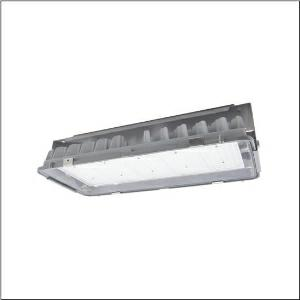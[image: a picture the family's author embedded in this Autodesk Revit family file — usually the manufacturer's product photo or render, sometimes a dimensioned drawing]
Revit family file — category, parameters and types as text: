
# Revit family: highbay_11xtreme_51hf82da4nma
name_source: partatom
category: Lighting Fixtures
units: mm (PartAtom-declared; Revit-internal decimal feet)

## family parameters
Cut with Voids When Loaded = No
Host = Face
Light Source = No
Part Type = Normal
Room Calculation Point = No
Round Connector Dimension = Use Diameter
Shared = No

## types (1)
- --- (1 x LED, 33700 lm, 187.7 W, 4000K)
    Apparent Load = 188 VA
    CIE Flux Codes = 84 96 100 100 100
    Color Rendering = 80
    Color Temperature = 4000K
    Default Elevation = 1800 mm
    Description = Highbay 11Xtreme, high bay luminaire, primary light control with lens, of PMMA, primary optical cover: cover, of toughened safety glass, light emission: direct distribution, primary light characteristic: symmetric, installation type: suspended mounting, surface-mounted, 1x LED module,for 1x LED, rated luminous flux: 33.700lm, luminous efficacy: 180lm/W, light colour: 840, colour temperature: 4000K, control gear: DALI 2, with cable H07RN-F 5x 1.5mm², mains connection: 220..240V, AC, 50/60Hz, cable length: 1,5m, rated input power: 188W, luminaire housing, of diecast aluminium, partly coated, silver, length: 595mm, width: 280mm, height: 195mm, protection rating (complete): IP66, insulation class (complete): insulation class I (protective earthing), certification: CE, ENEC, UKCA, protection symbol: D, ball protection: ball impact resistant according to DIN VDE 0710 part 13 (with chain suspension), impact resistance: IK08, permissible operating ambient temperature: -25..+45°C, reducing of maximum allowable ambient temperature of 5°C with ceiling mounting, packaging unit: 1 piece
    Height = 157 mm
    Lamp = 1 x LED
    Lamp Light Flux = 33700 lm
    Lamp Power = 187.7 W
    Lamp count = 1
    Length = 593 mm
    Luminous efficacy = 180 lm/W
    Manufacturer = Siteco
    ModVariant = No
    Model = 51HF82DA4NMA
    Mounting Place = Ceiling
    Mounting Type = Pendant
    Number of Poles = 1
    OnlyDefault = Yes
    Power Factor = 1
    Product Name = Highbay 11Xtreme
    Product group = high bay luminaire
    ProductGroupID = 901
    Protection Class = Protection class I
    Protection Degree = IP 66
    RLX_Detail_Level = 1
    RLX_Emergency_Light_Flux = 0 lm
    RLX_Emergency_Type = 0
    RLX_Emergency_Type_DB = No
    RlxData = <blob elided: 28357 chars, md5=3778f537>
    Socket = socket
    Standby Power = 0 W
    System Light Flux = 33700 lm
    System Power = 188 W
    Type Comments = factory setting: luminous flux: 100 % | dim-lin: 254 | 1255 mA
    Type Image = l_1258342.jpg
    URL = http://relux.com
    VarID = @adj_083152
    Voltage = 0 V
    Weight = 0.00 kg
    Width = 568 mm

## geometry (parser evidence)
native form markers: Blend x4, Sweep x8
no freeform markers — native parametric forms only
